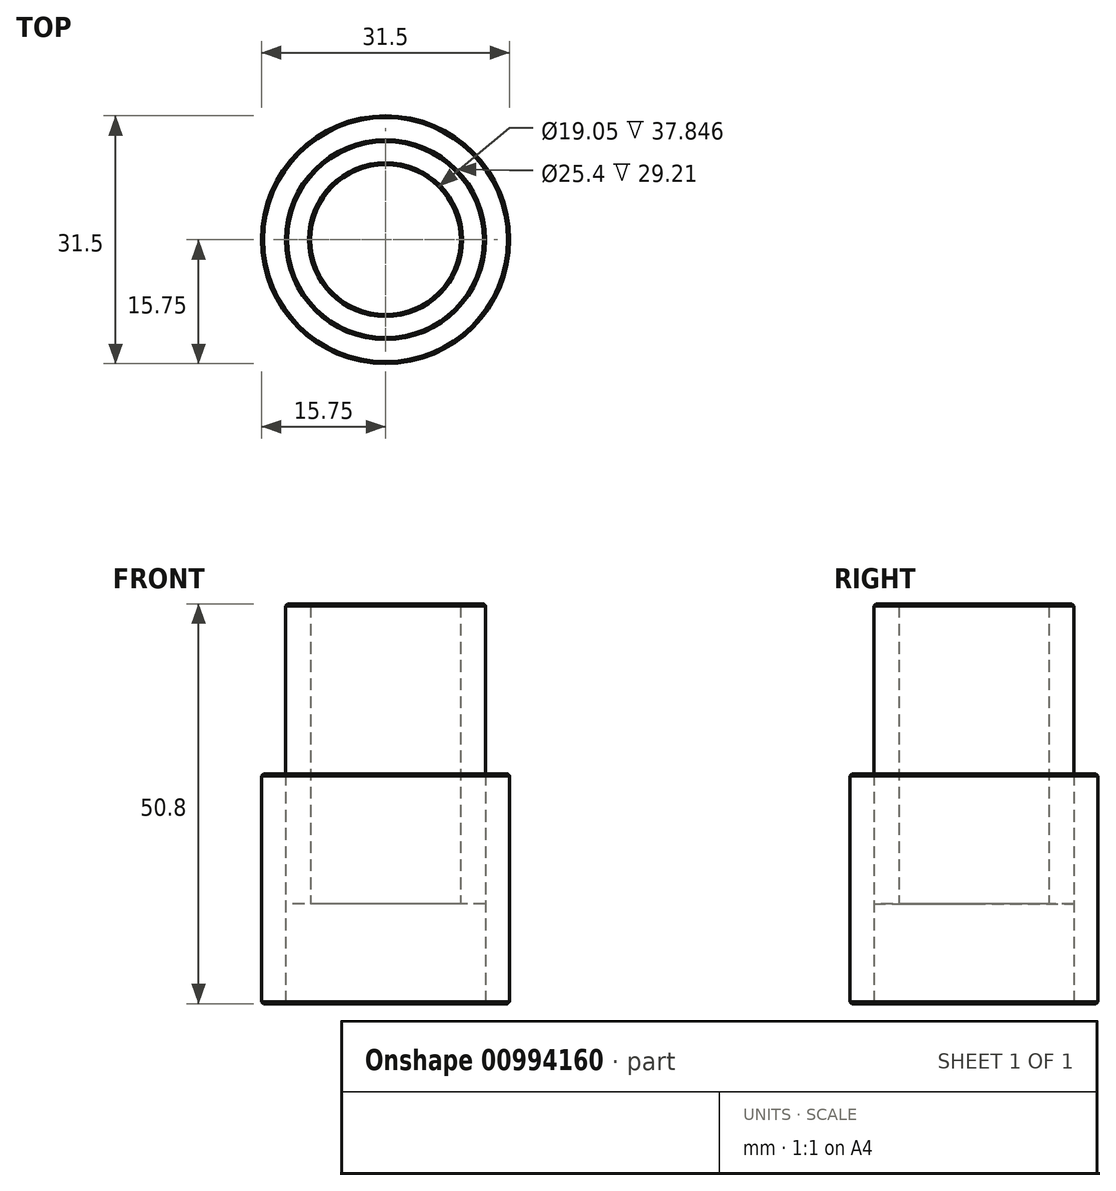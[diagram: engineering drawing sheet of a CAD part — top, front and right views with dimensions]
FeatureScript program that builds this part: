
annotation { "Feature Type Name" : "Feature", "Feature Type Description" : "" }
export const myFeature = defineFeature(function(context is Context, id is Id, definition is map)
    precondition{}
    {
        {
            var Q0;
            Q0=qCreatedBy(makeId("Top.planeOp"),FACE);
            var sketch = newSketch(context, id + "F0", { "sketchPlane" : qUnion([Q0])});
            skCircle(sketch, "E0", {"center": v(0, 0) * mm, "radius": 9.52 * mm});
            skCircle(sketch, "E1", {"center": v(0, 0) * mm, "radius": 12.7 * mm});
            skCircle(sketch, "E2", {"center": v(0, 0) * mm, "radius": 15.75 * mm});
            skSolve(sketch);
        }
        {
            var Q0;
            Q0=makeQuery(id+"F0.imprint","IMPRINT",FACE,{"disambiguationData":[TD([[makeQuery(id+"F0.imprint","IMPRINT",EDGE,{"derivedFrom":sQuery(id+"F0.wireOp",EDGE,"E1")}),-1.0]])]});
            extrude(context, id + "F1", {"entities" : qUnion([Q0]), "depth" : 29.2 * mm, "offsetDistance" : 25.4 * mm});
        }
        {
            var Q0;
            Q0=makeQuery(id+"F0.imprint","IMPRINT",FACE,{"disambiguationData":[TD([[makeQuery(id+"F0.imprint","IMPRINT",EDGE,{"derivedFrom":sQuery(id+"F0.wireOp",EDGE,"E0")}),-1.0]])]});
            extrude(context, id + "F2", {"entities" : qUnion([Q0]), "depth" : 50.8 * mm, "offsetDistance" : 25.4 * mm});
        }
        {
            var Q0;
            Q0=makeQuery(id+"F0.imprint","IMPRINT",FACE,{"disambiguationData":[TD([[makeQuery(id+"F0.imprint","IMPRINT",EDGE,{"derivedFrom":sQuery(id+"F0.wireOp",EDGE,"E0")}),-1.0]])]});
            extrude(context, id + "F3", {"entities" : qUnion([Q0]), "operationType" : NewBodyOperationType.REMOVE, "depth" : 12.7 * mm, "offsetDistance" : 25.4 * mm});
        }
        {
            var Q0;
            Q0=makeQuery(id+"F2.opExtrude","CAP_EDGE",EDGE,{"disambiguationData":[OSD([sQuery(id+"F0.wireOp",EDGE,"E1")])],"isStart":false});
            var Q1;
            Q1=makeQuery(id+"F2.opExtrude","CAP_EDGE",EDGE,{"disambiguationData":[OSD([sQuery(id+"F0.wireOp",EDGE,"E0")])],"isStart":false});
            var Q2;
            Q2=makeQuery(id+"F1.opExtrude","CAP_EDGE",EDGE,{"disambiguationData":[OSD([sQuery(id+"F0.wireOp",EDGE,"E2")])],"isStart":false});
            var Q3;
            Q3=makeQuery(id+"F1.opExtrude","CAP_EDGE",EDGE,{"disambiguationData":[OSD([sQuery(id+"F0.wireOp",EDGE,"E2")])],"isStart":true});
            chamfer(context, id + "F4", {"entities" : qUnion([Q0, Q1, Q2, Q3]), "width" : 0.25 * mm, "tangentPropagation" : true});
        }
    });
